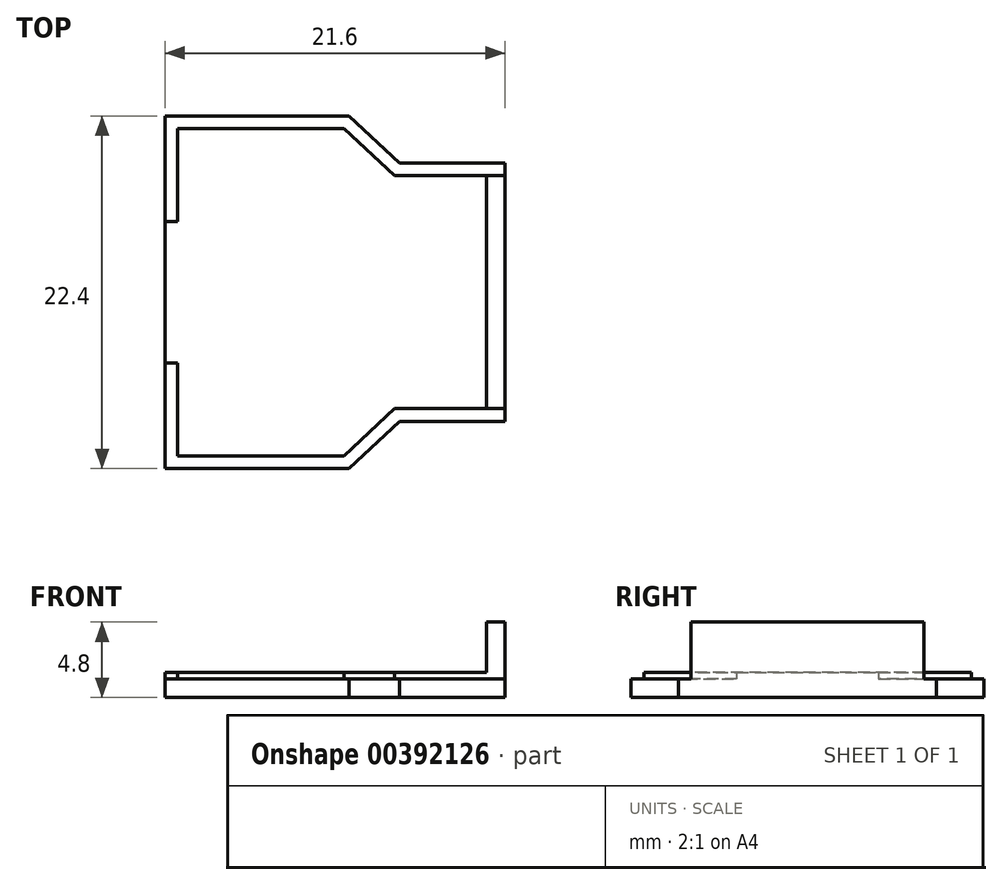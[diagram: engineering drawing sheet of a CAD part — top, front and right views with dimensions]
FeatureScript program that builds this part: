
annotation { "Feature Type Name" : "Feature", "Feature Type Description" : "" }
export const myFeature = defineFeature(function(context is Context, id is Id, definition is map)
    precondition{}
    {
        {
            var Q0;
            Q0=qCreatedBy(makeId("Top.planeOp"),FACE);
            var sketch = newSketch(context, id + "F0", { "sketchPlane" : qUnion([Q0])});
            skLineSegment(sketch, "E0.0", {"start": v(3.76, 8.2) * mm, "end": v(10.49, 8.2) * mm});
            skLineSegment(sketch, "E0.1", {"start": v(0.56, 11.2) * mm, "end": v(3.76, 8.2) * mm});
            skLineSegment(sketch, "E0.2", {"start": v(10.49, 8.2) * mm, "end": v(10.49, -8.2) * mm});
            skLineSegment(sketch, "E0.3", {"start": v(0.56, 11.2) * mm, "end": v(-11.11, 11.2) * mm});
            skLineSegment(sketch, "E0.4", {"start": v(-11.11, -11.2) * mm, "end": v(-11.11, 11.2) * mm});
            skLineSegment(sketch, "E0.7", {"start": v(0.56, -11.2) * mm, "end": v(3.76, -8.2) * mm});
            skLineSegment(sketch, "E0.8", {"start": v(0.56, -11.2) * mm, "end": v(-11.11, -11.2) * mm});
            skLineSegment(sketch, "E1.bottom", {"start": v(-11.11, 4.5) * mm, "end": v(-10.31, 4.5) * mm});
            skLineSegment(sketch, "E1.top", {"start": v(-11.11, -4.5) * mm, "end": v(-10.31, -4.5) * mm});
            skLineSegment(sketch, "E1.left", {"start": v(-11.11, 4.5) * mm, "end": v(-11.11, -4.5) * mm});
            skLineSegment(sketch, "E2.0", {"start": v(3.45, 7.4) * mm, "end": v(9.29, 7.4) * mm});
            skLineSegment(sketch, "E2.1", {"start": v(0.25, 10.4) * mm, "end": v(3.45, 7.4) * mm});
            skLineSegment(sketch, "E2.2", {"start": v(0.25, 10.4) * mm, "end": v(-10.31, 10.4) * mm});
            skLineSegment(sketch, "E2.3", {"start": v(-10.31, -10.4) * mm, "end": v(-10.31, 10.4) * mm});
            skLineSegment(sketch, "E2.6", {"start": v(0.25, -10.4) * mm, "end": v(3.45, -7.4) * mm});
            skLineSegment(sketch, "E2.7", {"start": v(0.25, -10.4) * mm, "end": v(-10.31, -10.4) * mm});
            skLineSegment(sketch, "E3", {"start": v(9.29, 7.4) * mm, "end": v(9.29, -7.4) * mm});
            skLineSegment(sketch, "E4", {"start": v(9.29, 7.4) * mm, "end": v(10.49, 7.4) * mm});
            skLineSegment(sketch, "E5", {"start": v(9.29, -7.4) * mm, "end": v(10.49, -7.4) * mm});
            skLineSegment(sketch, "E6", {"start": v(3.45, -7.4) * mm, "end": v(9.29, -7.4) * mm});
            skLineSegment(sketch, "E7", {"start": v(3.76, -8.2) * mm, "end": v(10.49, -8.2) * mm});
            skSolve(sketch);
        }
        {
            var Q0;
            Q0=makeQuery(id+"F0.imprint","IMPRINT",FACE,{"disambiguationData":[TD([[makeQuery(id+"F0.imprint","IMPRINT",EDGE,{"derivedFrom":sQuery(id+"F0.wireOp",EDGE,"E2.0")}),-1.0]])]});
            var Q1;
            {var subQ0=sQuery(id+"F0.wireOp",EDGE,"E1.bottom");Q1=makeQuery(id+"F0.imprint","IMPRINT",FACE,{"disambiguationData":[TD([[makeQuery(id+"F0.imprint","IMPRINT",EDGE,{"derivedFrom":subQ0}),-1.0]])]});}
            var Q2;
            Q2=makeQuery(id+"F0.imprint","IMPRINT",FACE,{"disambiguationData":[TD([[makeQuery(id+"F0.imprint","IMPRINT",EDGE,{"derivedFrom":sQuery(id+"F0.wireOp",EDGE,"E0.7")}),1.0]])]});
            var Q3;
            Q3=makeQuery(id+"F0.imprint","IMPRINT",FACE,{"disambiguationData":[TD([[makeQuery(id+"F0.imprint","IMPRINT",EDGE,{"derivedFrom":sQuery(id+"F0.wireOp",EDGE,"E3")}),1.0]])]});
            var Q4;
            {var subQ5=sQuery(id+"F0.wireOp",EDGE,"E0.0");Q4=makeQuery(id+"F0.imprint","IMPRINT",FACE,{"disambiguationData":[TD([[makeQuery(id+"F0.imprint","IMPRINT",EDGE,{"derivedFrom":subQ5}),-1.0]])]});}
            var Q5;
            Q5=sQuery(id+"F0.wireOp",EDGE,"E0.0");
            var Q6;
            Q6=sQuery(id+"F0.wireOp",EDGE,"E0.1");
            var Q7;
            Q7=sQuery(id+"F0.wireOp",EDGE,"E0.2");
            var Q8;
            Q8=sQuery(id+"F0.wireOp",EDGE,"E0.3");
            var Q9;
            Q9=sQuery(id+"F0.wireOp",EDGE,"E0.4");
            var Q10;
            Q10=sQuery(id+"F0.wireOp",EDGE,"E0.7");
            var Q11;
            Q11=sQuery(id+"F0.wireOp",EDGE,"E0.8");
            var Q12;
            Q12=sQuery(id+"F0.wireOp",EDGE,"E1.bottom");
            var Q13;
            Q13=sQuery(id+"F0.wireOp",EDGE,"E1.top");
            var Q14;
            Q14=sQuery(id+"F0.wireOp",EDGE,"E1.left");
            var Q15;
            Q15=sQuery(id+"F0.wireOp",EDGE,"E2.0");
            var Q16;
            Q16=sQuery(id+"F0.wireOp",EDGE,"E2.1");
            var Q17;
            Q17=sQuery(id+"F0.wireOp",EDGE,"E2.2");
            var Q18;
            Q18=sQuery(id+"F0.wireOp",EDGE,"E2.3");
            var Q19;
            Q19=sQuery(id+"F0.wireOp",EDGE,"E2.6");
            var Q20;
            Q20=sQuery(id+"F0.wireOp",EDGE,"E2.7");
            var Q21;
            Q21=sQuery(id+"F0.wireOp",EDGE,"E3");
            var Q22;
            Q22=sQuery(id+"F0.wireOp",EDGE,"E4");
            var Q23;
            Q23=sQuery(id+"F0.wireOp",EDGE,"E5");
            var Q24;
            Q24=sQuery(id+"F0.wireOp",EDGE,"E6");
            var Q25;
            Q25=sQuery(id+"F0.wireOp",EDGE,"E7");
            extrude(context, id + "F1", {"entities" : qUnion([Q0, Q1, Q2, Q3, Q4]), "surfaceEntities" : qUnion([Q5, Q6, Q7, Q8, Q9, Q10, Q11, Q12, Q13, Q14, Q15, Q16, Q17, Q18, Q19, Q20, Q21, Q22, Q23, Q24, Q25]), "depth" : 1.2 * mm});
        }
        {
            var Q0;
            {var subQ0=sQuery(id+"F0.wireOp",EDGE,"E1.bottom");Q0=makeQuery(id+"F0.imprint","IMPRINT",FACE,{"disambiguationData":[TD([[makeQuery(id+"F0.imprint","IMPRINT",EDGE,{"derivedFrom":subQ0}),-1.0]])]});}
            extrude(context, id + "F2", {"entities" : qUnion([Q0]), "operationType" : NewBodyOperationType.ADD, "depth" : 1.6 * mm});
        }
        {
            var Q0;
            Q0=makeQuery(id+"F0.imprint","IMPRINT",FACE,{"disambiguationData":[TD([[makeQuery(id+"F0.imprint","IMPRINT",EDGE,{"derivedFrom":sQuery(id+"F0.wireOp",EDGE,"E3")}),1.0]])]});
            extrude(context, id + "F3", {"entities" : qUnion([Q0]), "operationType" : NewBodyOperationType.ADD, "depth" : 4.8 * mm});
        }
        {
            var Q0;
            Q0=makeQuery(id+"F0.imprint","IMPRINT",FACE,{"disambiguationData":[TD([[makeQuery(id+"F0.imprint","IMPRINT",EDGE,{"derivedFrom":sQuery(id+"F0.wireOp",EDGE,"E2.0")}),-1.0]])]});
            extrude(context, id + "F4", {"entities" : qUnion([Q0]), "operationType" : NewBodyOperationType.ADD, "depth" : 1.6 * mm});
        }
    });
